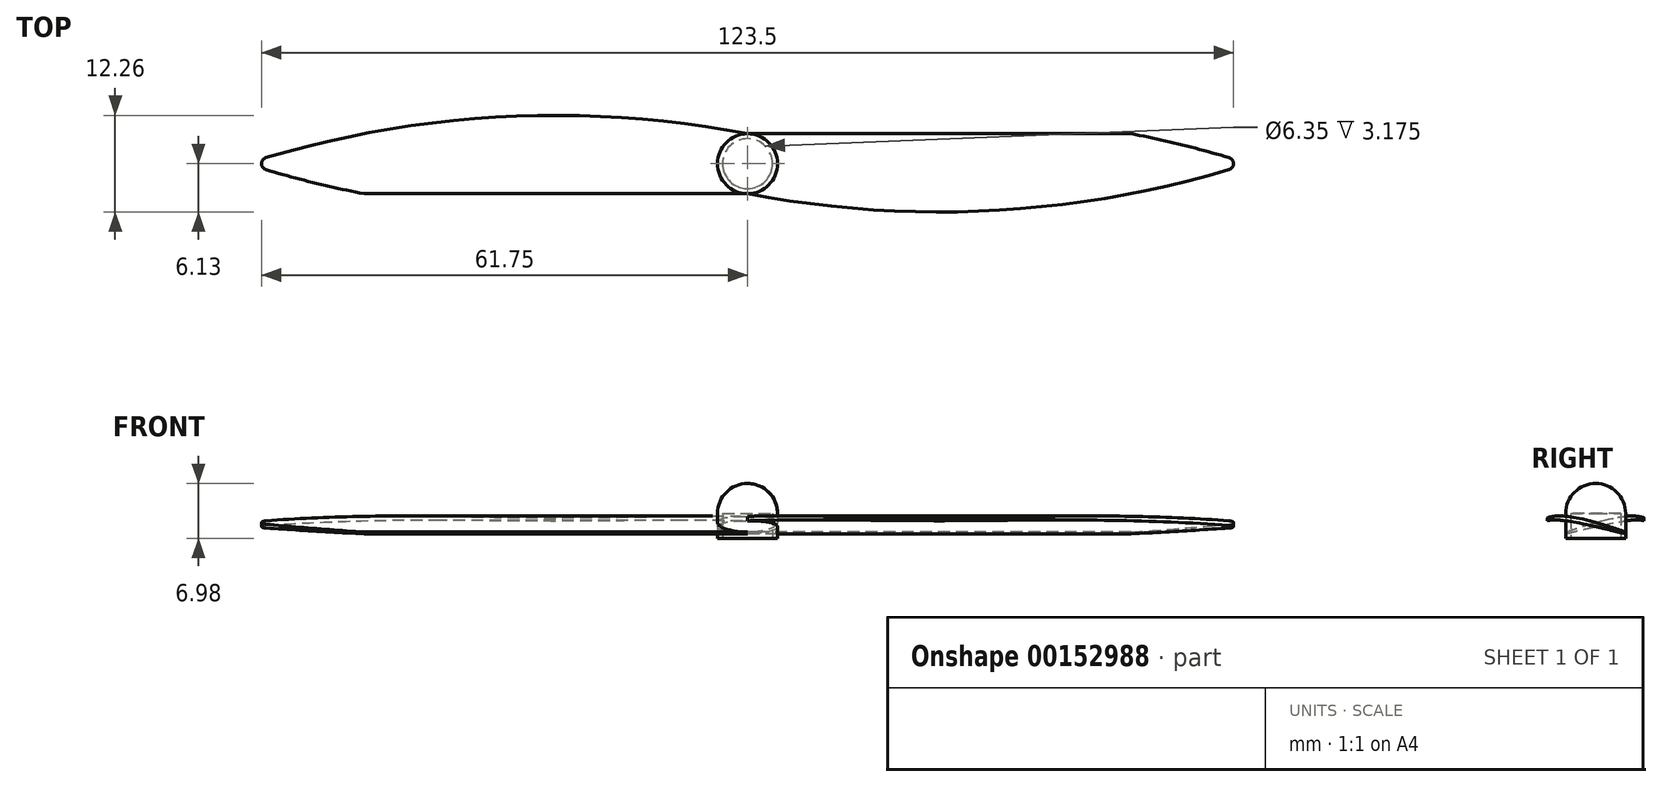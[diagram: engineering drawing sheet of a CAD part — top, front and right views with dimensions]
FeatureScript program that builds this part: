
annotation { "Feature Type Name" : "Feature", "Feature Type Description" : "" }
export const myFeature = defineFeature(function(context is Context, id is Id, definition is map)
    precondition{}
    {
        {
            var Q0;
            Q0=qCreatedBy(makeId("Top.planeOp"),FACE);
            var sketch = newSketch(context, id + "F0", { "sketchPlane" : qUnion([Q0])});
            skArc(sketch, "E0", {"start": v(0, 3.81) * mm, "mid": v(-3.81, 0) * mm, "end": v(0, -3.81) * mm});
            skArc(sketch, "E1", {"start": v(61.19, 0.75) * mm, "mid": v(30.78, 5.97) * mm, "end": v(0, 3.81) * mm});
            skArc(sketch, "E2.MirrorCS", {"start": v(61.19, -0.75) * mm, "mid": v(30.78, -5.97) * mm, "end": v(0, -3.81) * mm});
            skArc(sketch, "E3", {"start": v(61.19, -0.75) * mm, "mid": v(61.75, 0) * mm, "end": v(61.19, 0.75) * mm});
            skPoint(sketch, "E4.orphan", {"position": v(63.63, 0) * mm});
            skCircle(sketch, "E5", {"center": v(0, 0) * mm, "radius": 3.18 * mm});
            skSolve(sketch);
        }
        {
            var Q0;
            Q0 = qSketchRegion(id + "F0", true);
            extrude(context, id + "F1", {"entities" : qUnion([Q0]), "depth" : 3.17 * mm});
        }
        {
            var Q0;
            Q0=qCreatedBy(makeId("Right.planeOp"),FACE);
            var sketch = newSketch(context, id + "F2", { "sketchPlane" : qUnion([Q0])});
            skLineSegment(sketch, "E6.0.0", {"start": v(-3.81, 0) * mm, "end": v(3.81, 0) * mm});
            skLineSegment(sketch, "E6.0.2", {"start": v(3.81, 3.18) * mm, "end": v(-3.81, 3.18) * mm});
            skLineSegment(sketch, "E6.0.3", {"start": v(3.81, 0.8) * mm, "end": v(3.81, 0.59) * mm});
            skLineSegment(sketch, "E7", {"start": v(6.13, 3.18) * mm, "end": v(6.13, 0) * mm});
            skLineSegment(sketch, "E8", {"start": v(-6.13, 0) * mm, "end": v(-6.13, 3.18) * mm});
            skPoint(sketch, "E9.3.internal.snap0", {"position": v(-6.13, 1.59) * mm});
            skFitSpline(sketch, "E9", {"points": [v(6.13, 0) * mm, v(-2.04, 1.94) * mm, v(-6.13, 2.25) * mm, v(-7.08, 1.59) * mm], "startDerivative": vector(-17.73, 4.52) * mm, "endDerivative": vector(-4.2, -4.46) * mm});
            skFitSpline(sketch, "E10", {"points": [v(6.13, 0) * mm, v(-2.04, 2.54) * mm, v(-6.13, 2.63) * mm, v(-8.27, 1.21) * mm], "startDerivative": vector(-19.48, 6.83) * mm, "endDerivative": vector(-7.92, -6.98) * mm});
            skLineSegment(sketch, "E11", {"start": v(6.13, 3.18) * mm, "end": v(-6.13, 3.18) * mm});
            skLineSegment(sketch, "E12", {"start": v(6.13, 0) * mm, "end": v(-6.13, 0) * mm});
            skLineSegment(sketch, "E13", {"start": v(-6.13, 2.63) * mm, "end": v(-6.13, 2.25) * mm});
            skSolve(sketch);
        }
        {
            var Q0;
            {var subQ4=sQuery(id+"F2.wireOp",EDGE,"E7");Q0=makeQuery(id+"F2.imprint","IMPRINT",FACE,{"disambiguationData":[TD([[makeQuery(id+"F2.imprint","IMPRINT",EDGE,{"derivedFrom":subQ4}),-1.0]])]});}
            var Q1;
            {var subQ0=sQuery(id+"F2.wireOp",EDGE,"E12");var subQ1=sQuery(id+"F2.wireOp",EDGE,"E8");var subQ2=makeQuery(id+"F2.imprint","INTERSECT",VERTEX,{"derivedFrom":[subQ1,subQ0]});Q1=makeQuery(id+"F2.imprint","IMPRINT",FACE,{"disambiguationData":[TD([[makeQuery(id+"F2.imprint","IMPRINT",EDGE,{"disambiguationData":[TD([[subQ2,-1.0]])],"derivedFrom":subQ1}),-1.0]])]});}
            var Q2;
            {var subQ0=sQuery(id+"F2.wireOp",EDGE,"E6.0.3");Q2=makeQuery(id+"F2.imprint","IMPRINT",FACE,{"disambiguationData":[TD([[makeQuery(id+"F2.imprint","IMPRINT",EDGE,{"derivedFrom":subQ0}),1.0]])]});}
            extrude(context, id + "F3", {"entities" : qUnion([Q0, Q1, Q2]), "operationType" : NewBodyOperationType.REMOVE, "depth" : 132.71 * mm});
        }
        {
            var Q0;
            Q0=qCreatedBy(makeId("Right.planeOp"),FACE);
            var sketch = newSketch(context, id + "F4", { "sketchPlane" : qUnion([Q0])});
            skLineSegment(sketch, "E14", {"start": v(0, 0) * mm, "end": v(0, 34.95) * mm});
            skSolve(sketch);
        }
        {
            var Q0;
            Q0=makeQuery(id+"F1.opExtrude","SWEPT_BODY",BODY,{"disambiguationData":[OSD([sQuery(id+"F0.wireOp",EDGE,"E0"),sQuery(id+"F0.wireOp",EDGE,"E1"),sQuery(id+"F0.wireOp",EDGE,"E2.MirrorCS"),sQuery(id+"F0.wireOp",EDGE,"E3"),sQuery(id+"F0.wireOp",EDGE,"E5")])]});
            var Q1;
            Q1=sQuery(id+"F4.wireOp",EDGE,"E14");
            circularPattern(context, id + "F5", {"operationType" : NewBodyOperationType.ADD, "entities" : qUnion([Q0]), "axis" : qUnion([Q1]), "angle" : 360 * degree, "instanceCount" : 2, "equalSpace" : true});
        }
        {
            var Q0;
            Q0=qCreatedBy(makeId("Front.planeOp"),FACE);
            var sketch = newSketch(context, id + "F6", { "sketchPlane" : qUnion([Q0])});
            skLineSegment(sketch, "E15", {"start": v(-3.81, 0) * mm, "end": v(-3.81, 3.18) * mm});
            skLineSegment(sketch, "E16", {"start": v(3.81, 3.18) * mm, "end": v(3.81, 0) * mm});
            skLineSegment(sketch, "E17.0", {"start": v(-3.81, 3.18) * mm, "end": v(3.81, 3.18) * mm});
            skArc(sketch, "E18", {"start": v(3.81, 3.18) * mm, "mid": v(2.7, 5.87) * mm, "end": v(0, 6.99) * mm});
            skLineSegment(sketch, "E19", {"start": v(0, 3.18) * mm, "end": v(0, 9) * mm});
            skSolve(sketch);
        }
        {
            var Q0;
            Q0 = qSketchRegion(id + "F6", true);
            var Q1;
            Q1=sQuery(id+"F6.wireOp",EDGE,"E19");
            revolve(context, id + "F7", {"operationType" : NewBodyOperationType.ADD, "entities" : qUnion([Q0]), "axis" : qUnion([Q1]), "revolveType" : RevolveType.FULL});
        }
    });
